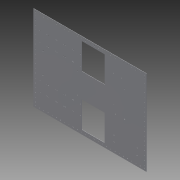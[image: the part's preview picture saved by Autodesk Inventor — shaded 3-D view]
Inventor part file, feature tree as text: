
AUTODESK INVENTOR PART (.ipt)
format: ipt  version: 2014 SP1 (Build 180222100, 222)  size: 348,672 bytes
history: native  units: in
note: dims shown in document units (in); Inventor stores cm internally (conversion verified against a paired STEP export)
features: reference x39, sketch x5, other x5, pattern_linear x2, sheet_metal_op x1
ambient origin geometry x8: Origin, YZ Plane, XZ Plane, XY Plane, X Axis, Y Axis, Z Axis, Center Point
bodies: Solid1 (feature_tree)
feature tree (52):
  sheet_metal_op  "Face1"
  pattern_linear  "Rectangular Pattern2"  Spacing1=7.25in  [1 undecoded]
  pattern_linear  "Rectangular Pattern5"  Spacing1=0.0625in  [1 undecoded]
  sketch  "Sketch1"  dims[d0=27.0in]
  other  "Plate1"
  sketch  "Sketch2"  dims[d1=20.325in]
  sketch  "Sketch4"  dims[d2=0.0625in]
  reference  "Reference4"
  reference  "Reference5"
  sketch  "Sketch12"  dims[d4=7.25in]
  reference  "Reference10"
  reference  "Reference11"
  sketch  "Sketch16"  dims[d5=5.5in d6=7.25in d17=0.0625in d18=0.0in d19=10.6299in d21=1.0in d23=1.0in d24=1.0in d65=0.0625in d66=0.0in d78=11.55in d79=5.5in d80=11.55in d97=0.0625in d98=0.0in d99=7.4803in d101=1.0in d102=0.7874in d104=26.0in d105=0.0625in d106=0.0in]
  reference  "Reference12"
  reference  "Reference13"
  reference  "Reference14"
  reference  "Reference15"
  reference  "Reference16"
  reference  "Reference17"
  reference  "Reference18"
  reference  "Reference19"
  reference  "Reference20"
  reference  "Reference21"
  reference  "Reference22"
  reference  "Reference23"
  reference  "Reference24"
  reference  "Reference25"
  reference  "Reference26"
  reference  "Reference27"
  reference  "Reference28"
  reference  "Reference29"
  reference  "Reference30"
  reference  "Reference31"
  reference  "Reference32"
  reference  "Reference33"
  reference  "Reference34"
  reference  "Reference35"
  reference  "Reference36"
  reference  "Reference37"
  reference  "Reference38"
  reference  "Reference39"
  reference  "Reference40"
  reference  "Reference41"
  reference  "Reference42"
  reference  "Reference43"
  reference  "Reference44"
  reference  "Reference45"
  reference  "Reference46"
  other  "Cut3"
  other  "Cut6"
  other  "Cut8"
  other  "Cut9"
note: 2 required parameter values undecoded (feature->parameter linkage not recoverable at this tier; creation-order binding heuristic only, values carry confidence <= 0.55)
